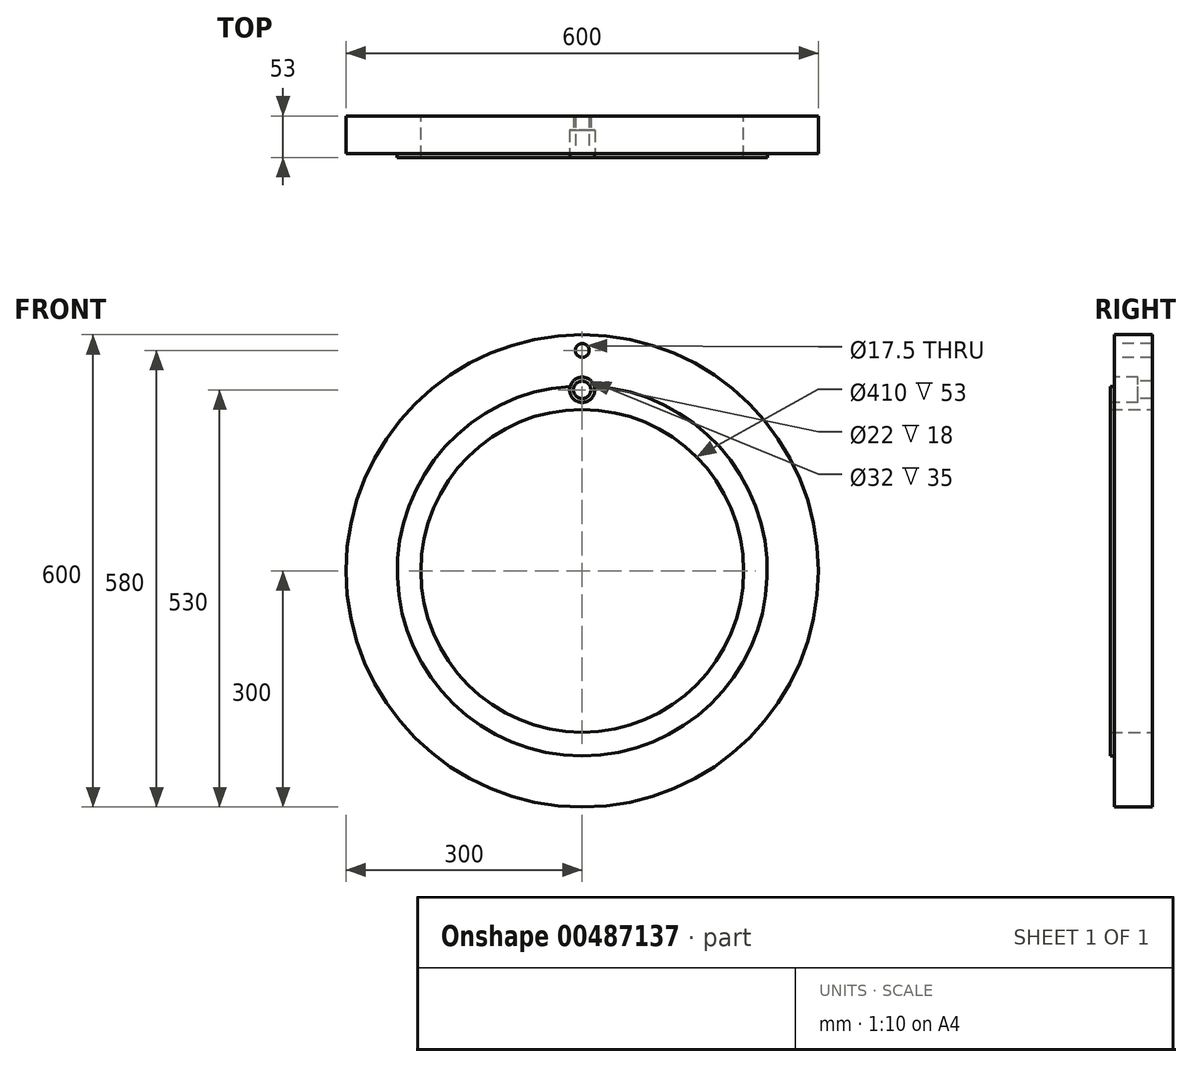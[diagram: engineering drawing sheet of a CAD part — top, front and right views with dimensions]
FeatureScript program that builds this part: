
annotation { "Feature Type Name" : "Feature", "Feature Type Description" : "" }
export const myFeature = defineFeature(function(context is Context, id is Id, definition is map)
    precondition{}
    {
        {
            var Q0;
            Q0=qCreatedBy(makeId("Front.planeOp"),FACE);
            var sketch = newSketch(context, id + "F0", { "sketchPlane" : qUnion([Q0])});
            skCircle(sketch, "E0", {"center": v(0, 0) * mm, "radius": 300 * mm});
            skSolve(sketch);
        }
        {
            var Q0;
            Q0 = qSketchRegion(id + "F0", true);
            var Q1;
            Q1=makeQuery(id+"F0.imprint","IMPRINT",FACE,{"disambiguationData":[TD([[makeQuery(id+"F0.imprint","IMPRINT",EDGE,{"derivedFrom":sQuery(id+"F0.wireOp",EDGE,"E0")}),1.0]])]});
            extrude(context, id + "F1", {"entities" : qUnion([Q0, Q1]), "depth" : 48 * mm});
        }
        {
            var Q0;
            Q0=makeQuery(id+"F1.opExtrude","CAP_FACE",FACE,{"disambiguationData":[OSD([sQuery(id+"F0.wireOp",EDGE,"E0")])],"isStart":false});
            var sketch = newSketch(context, id + "F2", { "sketchPlane" : qUnion([Q0])});
            skCircle(sketch, "E1", {"center": v(0, 0) * mm, "radius": 235 * mm});
            skSolve(sketch);
        }
        {
            var Q0;
            Q0=makeQuery(id+"F2.imprint","IMPRINT",FACE,{"disambiguationData":[TD([[makeQuery(id+"F2.imprint","IMPRINT",EDGE,{"derivedFrom":sQuery(id+"F2.wireOp",EDGE,"E1")}),1.0]])]});
            extrude(context, id + "F3", {"entities" : qUnion([Q0]), "operationType" : NewBodyOperationType.ADD, "depth" : 5 * mm});
        }
        {
            var Q0;
            Q0=makeQuery(id+"F1.opExtrude","CAP_FACE",FACE,{"disambiguationData":[OSD([sQuery(id+"F0.wireOp",EDGE,"E0")])],"isStart":false});
            var sketch = newSketch(context, id + "F4", { "sketchPlane" : qUnion([Q0])});
            skCircle(sketch, "E2", {"center": v(0, 0) * mm, "radius": 280 * mm, "construction": true});
            skLineSegment(sketch, "E3", {"start": v(0, 0) * mm, "end": v(0, 280) * mm, "construction": true});
            skSolve(sketch);
        }
        {
            var Q0;
            Q0=sQuery(id+"F4.wireOp",VERTEX,"E3.end");
            var Q1;
            Q1=makeQuery(id+"F1.opExtrude","SWEPT_BODY",BODY,{"disambiguationData":[OSD([sQuery(id+"F0.wireOp",EDGE,"E0")])]});
            hole(context, id + "F5", {"style" : HoleStyle.SIMPLE, "endStyle" : HoleEndStyle.THROUGH, "holeDiameter" : 17.5 * mm, "isTappedThrough" : true, "tappedDepth" : 12 * mm, "tapClearance" : 3, "locations" : qUnion([Q0]), "scope" : qUnion([Q1])});
        }
        {
            var Q0;
            Q0=makeQuery(id+"F1.opExtrude","CAP_FACE",FACE,{"disambiguationData":[OSD([sQuery(id+"F0.wireOp",EDGE,"E0")])],"isStart":true});
            var sketch = newSketch(context, id + "F6", { "sketchPlane" : qUnion([Q0])});
            skCircle(sketch, "E4", {"center": v(0, 0) * mm, "radius": 205 * mm});
            skSolve(sketch);
        }
        {
            var Q0;
            Q0=makeQuery(id+"F6.imprint","IMPRINT",FACE,{"disambiguationData":[TD([[makeQuery(id+"F6.imprint","IMPRINT",EDGE,{"derivedFrom":sQuery(id+"F6.wireOp",EDGE,"E4")}),1.0]])]});
            extrude(context, id + "F7", {"entities" : qUnion([Q0]), "operationType" : NewBodyOperationType.REMOVE, "endBound" : BoundingType.THROUGH_ALL, "oppositeDirection" : true, "depth" : 25 * mm});
        }
        {
            var Q0;
            Q0=makeQuery(id+"F3.opExtrude","CAP_FACE",FACE,{"disambiguationData":[OSD([sQuery(id+"F2.wireOp",EDGE,"E1")])],"isStart":false});
            var sketch = newSketch(context, id + "F8", { "sketchPlane" : qUnion([Q0])});
            skCircle(sketch, "E5", {"center": v(0, 0) * mm, "radius": 230 * mm, "construction": true});
            skLineSegment(sketch, "E6", {"start": v(0, 0) * mm, "end": v(0, 230) * mm, "construction": true});
            skSolve(sketch);
        }
        {
            var Q0;
            Q0=sQuery(id+"F8.wireOp",VERTEX,"E6.end");
            var Q1;
            Q1=makeQuery(id+"F1.opExtrude","SWEPT_BODY",BODY,{"disambiguationData":[OSD([sQuery(id+"F0.wireOp",EDGE,"E0")])]});
            hole(context, id + "F9", {"style" : HoleStyle.C_BORE, "endStyle" : HoleEndStyle.THROUGH, "holeDiameter" : 22 * mm, "cBoreDiameter" : 32 * mm, "cBoreDepth" : 30 * mm, "isTappedThrough" : true, "tappedDepth" : 12 * mm, "tapClearance" : 3, "locations" : qUnion([Q0]), "scope" : qUnion([Q1])});
        }
    });
